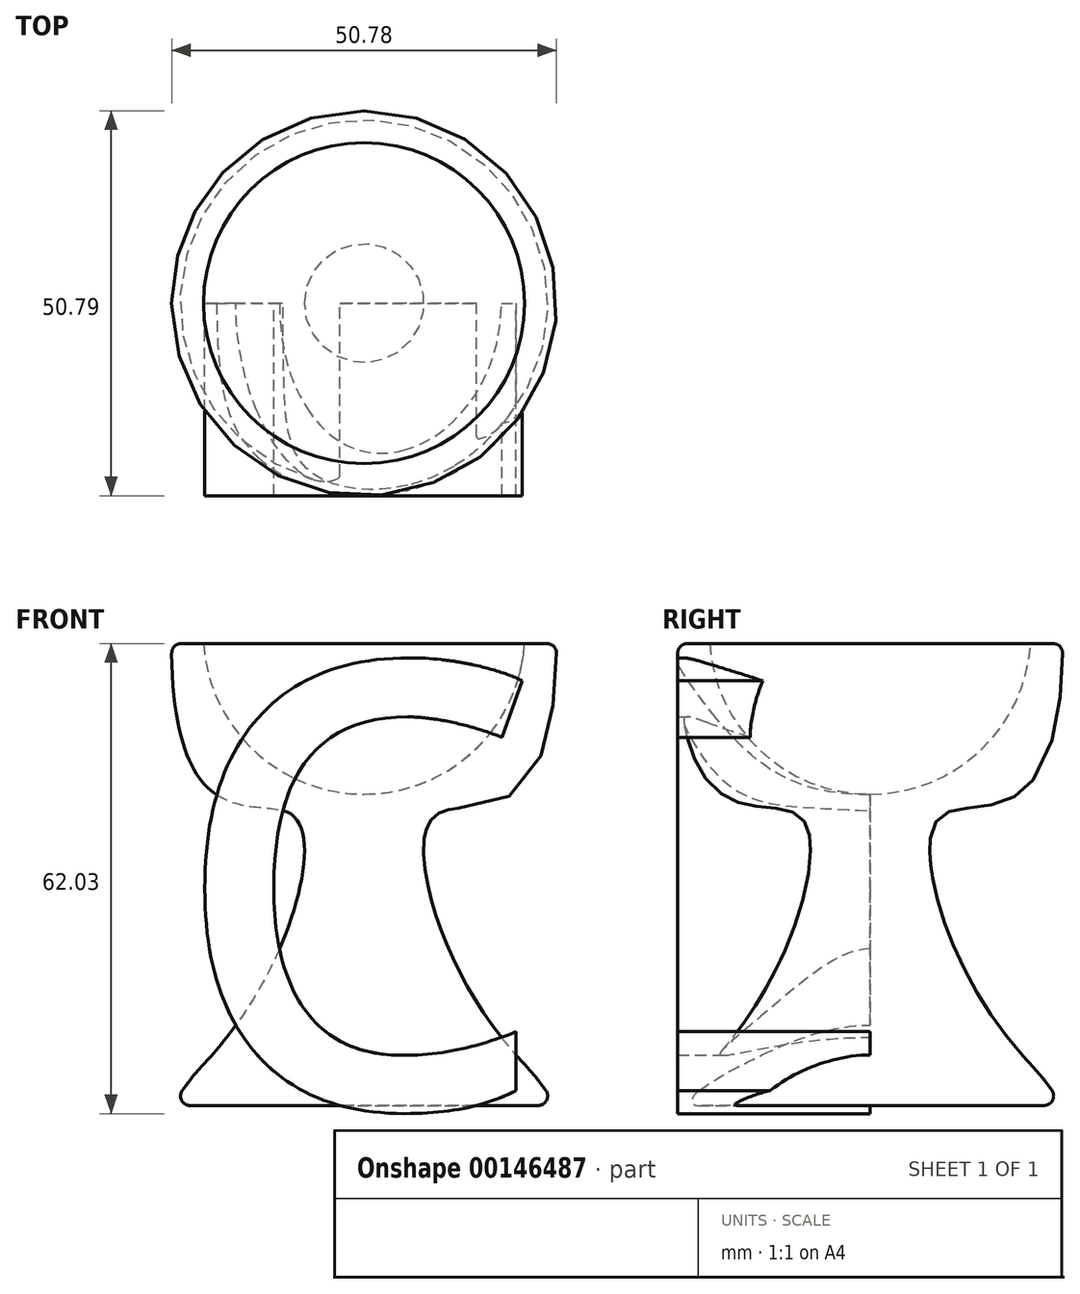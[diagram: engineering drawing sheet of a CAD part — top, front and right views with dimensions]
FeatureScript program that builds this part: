
annotation { "Feature Type Name" : "Feature", "Feature Type Description" : "" }
export const myFeature = defineFeature(function(context is Context, id is Id, definition is map)
    precondition{}
    {
        {
            var Q0;
            Q0=qCreatedBy(makeId("Top.planeOp"),FACE);
            var sketch = newSketch(context, id + "F0", { "sketchPlane" : qUnion([Q0])});
            skCircle(sketch, "E0", {"center": v(0, 0) * mm, "radius": 25.4 * mm});
            skSolve(sketch);
        }
        {
            var Q0;
            Q0 = qSketchRegion(id + "F0", true);
            extrude(context, id + "F1", {"entities" : qUnion([Q0]), "depth" : 60.96 * mm});
        }
        {
            var Q0;
            Q0=qCreatedBy(makeId("Right.planeOp"),FACE);
            var sketch = newSketch(context, id + "F2", { "sketchPlane" : qUnion([Q0])});
            skLineSegment(sketch, "E1", {"start": v(25.4, 68.5) * mm, "end": v(25.4, -46.1) * mm});
            skLineSegment(sketch, "E2", {"start": v(0, 69.5) * mm, "end": v(0, -43.72) * mm, "construction": true});
            skLineSegment(sketch, "E3", {"start": v(57.3, 60.96) * mm, "end": v(-44.62, 60.96) * mm, "construction": true});
            skFitSpline(sketch, "E4", {"points": [v(25.4, 60.96) * mm, v(9.52, 38.37) * mm, v(11.3, 20.32) * mm, v(20.42, 6.25) * mm, v(25.4, 0) * mm], "startDerivative": vector(0, -251.03) * mm, "endDerivative": vector(48.76, -70.92) * mm});
            skLineSegment(sketch, "E5", {"start": v(25.4, 34.2) * mm, "end": v(25.4, 0) * mm});
            skSolve(sketch);
        }
        {
            var Q0;
            Q0 = qSketchRegion(id + "F2", true);
            var Q1;
            Q1=sQuery(id+"F2.wireOp",EDGE,"E2");
            revolve(context, id + "F3", {"operationType" : NewBodyOperationType.REMOVE, "entities" : qUnion([Q0]), "axis" : qUnion([Q1]), "revolveType" : RevolveType.FULL, "oppositeDirection" : true});
        }
        {
            var Q0;
            Q0=qCreatedBy(makeId("Front.planeOp"),FACE);
            var sketch = newSketch(context, id + "F4", { "sketchPlane" : qUnion([Q0])});
            skText(sketch, "E6", { "text": "c\n", "fontName": "OpenSans-Regular.ttf"});
            const initialGuessF4  = {"E6": [-0.0271, 0, 1, 0, 0.07803]};
            skSetInitialGuess(sketch, initialGuessF4);
            skSolve(sketch);
        }
        {
            var Q0;
            Q0 = qSketchRegion(id + "F4", true);
            extrude(context, id + "F5", {"entities" : qUnion([Q0]), "operationType" : NewBodyOperationType.ADD, "depth" : 25.4 * mm});
        }
        {
            var Q0;
            Q0=qCreatedBy(makeId("Front.planeOp"),FACE);
            var sketch = newSketch(context, id + "F6", { "sketchPlane" : qUnion([Q0])});
            skArc(sketch, "E7", {"start": v(0, 41.09) * mm, "mid": v(21.22, 62.3) * mm, "end": v(0, 83.53) * mm});
            skLineSegment(sketch, "E8", {"start": v(0, 83.53) * mm, "end": v(0, 41.09) * mm});
            skLineSegment(sketch, "E9", {"start": v(0, 62.3) * mm, "end": v(0, 62.3) * mm});
            skSolve(sketch);
        }
        {
            var Q0;
            Q0 = qSketchRegion(id + "F6", true);
            var Q1;
            Q1=sQuery(id+"F6.wireOp",EDGE,"E8");
            revolve(context, id + "F7", {"operationType" : NewBodyOperationType.REMOVE, "entities" : qUnion([Q0]), "axis" : qUnion([Q1]), "revolveType" : RevolveType.FULL});
        }
        {
            var Q0;
            Q0=makeQuery(id+"F3.boolean.opBoolean","MERGE",EDGE,{"derivedFrom":[makeQuery(id+"F1.opExtrude","CAP_EDGE",EDGE,{"disambiguationData":[OSD([sQuery(id+"F0.wireOp",EDGE,"E0")])],"isStart":false}),makeQuery(id+"F3.opRevolve","SWEPT_EDGE",EDGE,{"disambiguationData":[OSD([sQuery(id+"F2.wireOp",EDGE,"E1"),sQuery(id+"F2.wireOp",EDGE,"E4")])]})]});
            fillet(context, id + "F8", {"entities" : qUnion([Q0]), "radius" : 1.27 * mm, "tangentPropagation" : true, "allowEdgeOverflow" : false});
        }
        {
            var Q0;
            Q0=makeQuery(id+"F3.boolean.opBoolean","MERGE",EDGE,{"derivedFrom":[makeQuery(id+"F1.opExtrude","CAP_EDGE",EDGE,{"disambiguationData":[OSD([sQuery(id+"F0.wireOp",EDGE,"E0")])],"isStart":true}),makeQuery(id+"F3.opRevolve","SWEPT_EDGE",EDGE,{"disambiguationData":[OSD([sQuery(id+"F2.wireOp",EDGE,"E4"),sQuery(id+"F2.wireOp",EDGE,"E5")])]})]});
            fillet(context, id + "F9", {"entities" : qUnion([Q0]), "radius" : 1.27 * mm, "tangentPropagation" : true, "allowEdgeOverflow" : false});
        }
    });
